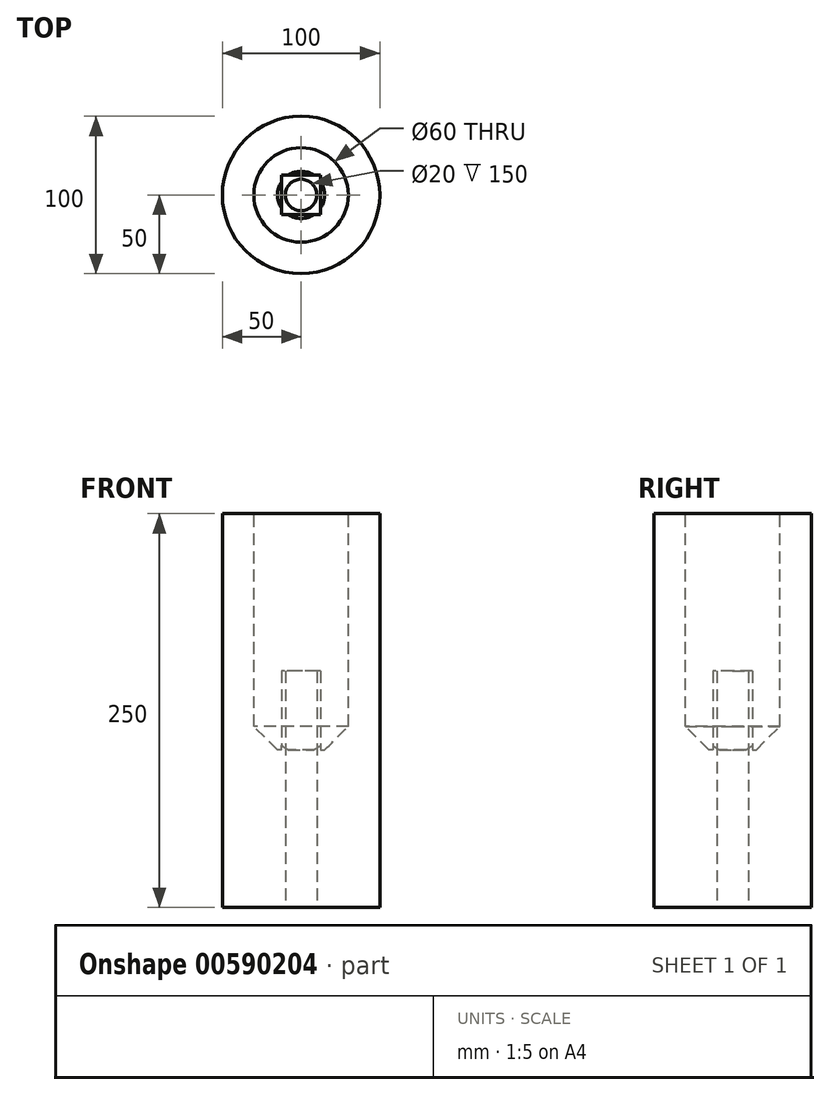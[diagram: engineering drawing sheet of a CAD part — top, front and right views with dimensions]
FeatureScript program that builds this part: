
annotation { "Feature Type Name" : "Feature", "Feature Type Description" : "" }
export const myFeature = defineFeature(function(context is Context, id is Id, definition is map)
    precondition{}
    {
        {
            var Q0;
            Q0=qCreatedBy(makeId("Top.planeOp"),FACE);
            var sketch = newSketch(context, id + "F0", { "sketchPlane" : qUnion([Q0])});
            skCircle(sketch, "E0", {"center": v(0, 0) * mm, "radius": 50 * mm});
            skSolve(sketch);
        }
        {
            var Q0;
            Q0=makeQuery(id+"F0.imprint","IMPRINT",FACE,{"disambiguationData":[TD([[makeQuery(id+"F0.imprint","IMPRINT",EDGE,{"derivedFrom":sQuery(id+"F0.wireOp",EDGE,"E0")}),1.0]])]});
            extrude(context, id + "F1", {"entities" : qUnion([Q0]), "depth" : 200 * mm, "offsetDistance" : 25 * mm});
        }
        {
            var Q0;
            Q0=makeQuery(id+"F1.opExtrude","CAP_FACE",FACE,{"disambiguationData":[OSD([sQuery(id+"F0.wireOp",EDGE,"E0")])],"isStart":false});
            var sketch = newSketch(context, id + "F2", { "sketchPlane" : qUnion([Q0])});
            skCircle(sketch, "E1", {"center": v(0, 0) * mm, "radius": 30 * mm});
            skSolve(sketch);
        }
        {
            var Q0;
            Q0 = qSketchRegion(id + "F2", true);
            extrude(context, id + "F3", {"entities" : qUnion([Q0]), "operationType" : NewBodyOperationType.REMOVE, "oppositeDirection" : true, "depth" : 150 * mm, "offsetDistance" : 25 * mm});
        }
        {
            var Q0;
            Q0=makeQuery(id+"F1.opExtrude","CAP_FACE",FACE,{"disambiguationData":[OSD([sQuery(id+"F0.wireOp",EDGE,"E0")])],"isStart":true});
            var sketch = newSketch(context, id + "F4", { "sketchPlane" : qUnion([Q0])});
            skCircle(sketch, "E2", {"center": v(0, 0) * mm, "radius": 10 * mm});
            skSolve(sketch);
        }
        {
            var Q0;
            Q0=makeQuery(id+"F1.opExtrude","CAP_FACE",FACE,{"disambiguationData":[OSD([sQuery(id+"F0.wireOp",EDGE,"E0")])],"isStart":true});
            var Q1;
            Q1=makeQuery(id+"F4.imprint","IMPRINT",FACE,{"disambiguationData":[TD([[makeQuery(id+"F4.imprint","IMPRINT",EDGE,{"derivedFrom":sQuery(id+"F4.wireOp",EDGE,"E2")}),1.0]])]});
            extrude(context, id + "F5", {"entities" : qUnion([Q0, Q1]), "operationType" : NewBodyOperationType.ADD, "depth" : 50 * mm, "offsetDistance" : 25 * mm});
        }
        {
            var Q0;
            Q0=makeQuery(id+"F5.opExtrude","CAP_FACE",FACE,{"disambiguationData":[OSD([sQuery(id+"F0.wireOp",EDGE,"E0")])],"isStart":false});
            var sketch = newSketch(context, id + "F6", { "sketchPlane" : qUnion([Q0])});
            skCircle(sketch, "E3", {"center": v(0, 0) * mm, "radius": 10 * mm});
            skSolve(sketch);
        }
        {
            var Q0;
            Q0=makeQuery(id+"F6.imprint","IMPRINT",FACE,{"disambiguationData":[TD([[makeQuery(id+"F6.imprint","IMPRINT",EDGE,{"derivedFrom":sQuery(id+"F6.wireOp",EDGE,"E3")}),1.0]])]});
            extrude(context, id + "F7", {"entities" : qUnion([Q0]), "operationType" : NewBodyOperationType.REMOVE, "oppositeDirection" : true, "depth" : 150 * mm, "offsetDistance" : 25 * mm});
        }
        {
            var Q0;
            Q0=makeQuery(id+"F3.boolean.opBoolean","COPY",FACE,{"derivedFrom":makeQuery(id+"F3.opExtrude","CAP_FACE",FACE,{"disambiguationData":[OSD([sQuery(id+"F2.wireOp",EDGE,"E1")])],"isStart":false})});
            var sketch = newSketch(context, id + "F8", { "sketchPlane" : qUnion([Q0])});
            skLineSegment(sketch, "E4.bottom", {"start": v(12.5, 12.5) * mm, "end": v(-12.5, 12.5) * mm});
            skLineSegment(sketch, "E4.top", {"start": v(12.5, -12.5) * mm, "end": v(-12.5, -12.5) * mm});
            skLineSegment(sketch, "E4.left", {"start": v(12.5, 12.5) * mm, "end": v(12.5, -12.5) * mm});
            skLineSegment(sketch, "E4.right", {"start": v(-12.5, 12.5) * mm, "end": v(-12.5, -12.5) * mm});
            skPoint(sketch, "E4.middle", {"position": v(0, 0) * mm});
            skSolve(sketch);
        }
        {
            var Q0;
            Q0=makeQuery(id+"F8.imprint","IMPRINT",FACE,{"disambiguationData":[TD([[makeQuery(id+"F8.imprint","IMPRINT",EDGE,{"derivedFrom":sQuery(id+"F8.wireOp",EDGE,"E4.bottom")}),1.0]])]});
            extrude(context, id + "F9", {"entities" : qUnion([Q0]), "operationType" : NewBodyOperationType.ADD, "depth" : 50 * mm, "offsetDistance" : 25 * mm});
        }
        {
            var Q0;
            Q0=makeQuery(id+"F3.boolean.opBoolean","COPY",EDGE,{"derivedFrom":makeQuery(id+"F3.opExtrude","CAP_EDGE",EDGE,{"disambiguationData":[OSD([sQuery(id+"F2.wireOp",EDGE,"E1")])],"isStart":false})});
            chamfer(context, id + "F10", {"entities" : qUnion([Q0]), "width" : 15 * mm, "tangentPropagation" : true});
        }
    });
